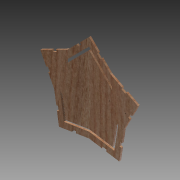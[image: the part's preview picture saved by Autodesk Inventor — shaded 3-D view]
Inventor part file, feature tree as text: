
AUTODESK INVENTOR PART (.ipt)
format: ipt  version: 2015 (Build 190159000, 159)  size: 225,280 bytes
history: native  units: in
note: dims shown in document units (in); Inventor stores cm internally (conversion verified against a paired STEP export)
features: sketch x4, extrude x3, other x2
ambient origin geometry x8: Origin, YZ Plane, XZ Plane, XY Plane, X Axis, Y Axis, Z Axis, Center Point
bodies: Solid1 (feature_tree)
feature tree (9):
  extrude  "Extrusion1"  Depth=7.0in
  extrude  "Extrusion2"  Depth=1.9685in TaperAngle=360.0deg
  sketch  "Sketch3"  dims[d10=0.125in d11=0.0in d12=0.15in]
  other  "Work Axis1"
  other  "Work Axis2"
  extrude  "Extrusion3"  Depth=0.15in
  sketch  "Sketch1"  dims[d0=5.0in d1=7.0in]
  sketch  "Sketch2"  dims[d2=1.9685in d4=360.0deg d6=1.9685in d8=360.0deg]
  sketch  "Sketch4"  dims[d13=0.15in d14=0.125in d15=0.15in d16=0.3in d18=0.15in d20=1.0in d21=0.0in d22=3.5in d23=7.1937in d24=0.15in d26=0.4in d27=0.4in d29=0.15in d30=0.1in d32=0.1in d33=0.15in d34=0.15in d35=0.15in d36=0.15in d37=0.4in d38=0.4in d39=0.4in d40=0.4in d44=45.0deg d45=45.0deg d46=45.0deg d47=45.0deg d48=0.1in d50=0.1in d51=1.0in d52=0.0in]
